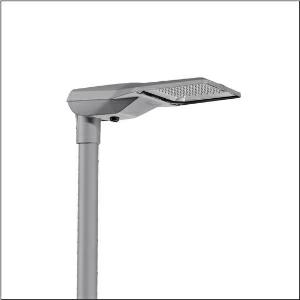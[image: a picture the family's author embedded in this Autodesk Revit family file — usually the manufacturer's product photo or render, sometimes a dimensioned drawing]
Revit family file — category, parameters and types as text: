
# Revit family: streetlight_sl_21_iq_midi___st1_0a_5xe3d31u08mb_cc74
name_source: partatom
category: Lighting Fixtures
units: mm (PartAtom-declared; Revit-internal decimal feet)

## family parameters
Cut with Voids When Loaded = No
Host = Face
Light Source = No
Part Type = Normal
Room Calculation Point = No
Round Connector Dimension = Use Diameter
Shared = No

## types (1)
- --- (1 x LED, 18340 lm, 129.3 W, 3000K)
    Apparent Load = 129 VA
    CIE Flux Codes = 37 72 97 100 100
    Color Rendering = 70
    Color Temperature = 3000K
    Default Elevation = 1800 mm
    Description = Streetlight SL 21 iQ midi, mast luminaire, primary light control with lens, of PMMA, primary optical cover: cover, of toughened safety glass, transparent, light distribution: ST1.0a, light emission: direct distribution, primary light characteristic: asymmetric, installation type: post-top, side-entry, LED, High Power LED, rated luminous flux: 18.340lm, luminous efficacy: 142lm/W, light colour: 730, colour temperature: 3000K, control: pre-setting: logarithmic dimming characteristic, Street-Remote, Auto-Match, Temp-Guard, Lumen-Switch, Night-Set, Smart-Wire, Light-Fading, Desk-Remote (wireless, voltage-free reading and setting of iQ features in the workshop via application-optimized NFC function/RFID function), optimised constant luminous flux control (CLO 2.0), mains connection: 230..240V, AC, 50/60Hz, start of lifetime: 129W, end of service life: 142W, reduction: 56W, luminaire housing, of diecast aluminium, powder-coated, Siteco® metallic grey (DB 702S), corrosivity category C5 mid according to DIN EN ISO 12944, please order mast flange separately, inclination adjustable: 0°, 5°, 10°, 15°, sealing non-destructively replaceable, multi-level sealing system, length: 644mm, width: 335mm, height: 110mm, mast flange for spigot size: 42mm (side-entry): 5XC10008XM4, 60/48mm (side-entry/post-top): 5XC10108XM2, 76/60mm (side-entry/post-top): 5XC10108XM1, Smart Interface below, protection rating (complete): IP66, insulation class (complete): insulation class II (safety insulation), certification: CE, ENEC, ENEC+, VDE, impact resistance: IK09, permissible operating ambient temperature for outdoor applications: -40..+50°C, standard-compliant lighting for roads and squares, packaging unit: 1 piece

Light Distribution: ST1.0a
    Height = 111 mm
    Lamp = 1 x LED
    Lamp Light Flux = 18340 lm
    Lamp Power = 129.3 W
    Lamp count = 1
    Length = 644 mm
    Luminous efficacy = 142 lm/W
    Manufacturer = Siteco
    ModVariant = No
    Model = 5XE3D31U08MB
    Number of Poles = 1
    OnlyDefault = Yes
    Power Factor = 1
    Product Name = Streetlight SL 21 iQ midi | ST1.0a
    Product group = mast luminaire | pylon top
    ProductGroupID = 6100
    Protection Class = Protection class II
    Protection Degree = IP 66
    RLX_Detail_Level = 1
    RLX_Emergency_Light_Flux = 0 lm
    RLX_Emergency_Type = 0
    RLX_Emergency_Type_DB = No
    RlxData = <blob elided: 90713 chars, md5=e40f12e8>
    Socket = socket
    Standby Power = 0 W
    System Light Flux = 18340 lm
    System Power = 129 W
    Type Comments = factory setting: luminous flux: 100 % | dim-lin: 254 | 672 mA
    Type Image = l_1004300.jpg
    URL = http://relux.com
    VarID = @adj_083529
    Voltage = 0 V
    Weight = 0.00 kg
    Width = 336 mm

## geometry (parser evidence)
native form markers: Blend x4, Sweep x11
no freeform markers — native parametric forms only
